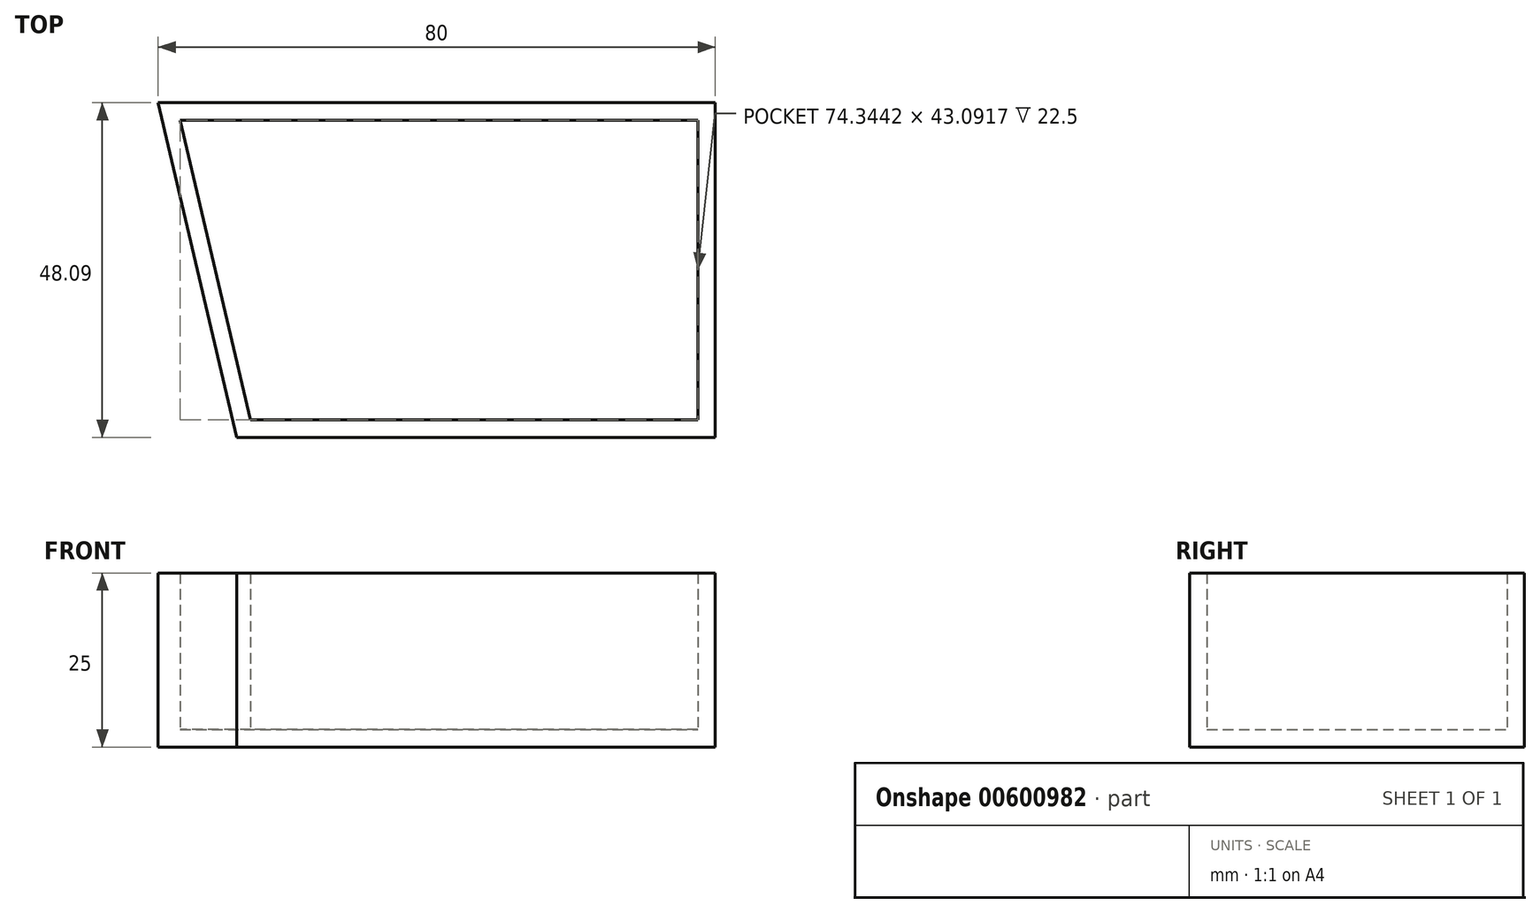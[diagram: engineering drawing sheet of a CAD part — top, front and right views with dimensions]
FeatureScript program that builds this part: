
annotation { "Feature Type Name" : "Feature", "Feature Type Description" : "" }
export const myFeature = defineFeature(function(context is Context, id is Id, definition is map)
    precondition{}
    {
        {
            var Q0;
            Q0=qCreatedBy(makeId("Top.planeOp"),FACE);
            var sketch = newSketch(context, id + "F0", { "sketchPlane" : qUnion([Q0])});
            skLineSegment(sketch, "E0", {"start": v(-43.5, 48.1) * mm, "end": v(36.5, 48.1) * mm});
            skLineSegment(sketch, "E1", {"start": v(36.5, 48.85) * mm, "end": v(36.5, 0) * mm});
            skLineSegment(sketch, "E2", {"start": v(36.5, 0) * mm, "end": v(-32.19, 0) * mm});
            skLineSegment(sketch, "E3", {"start": v(-32.19, 0) * mm, "end": v(-43.5, 48.1) * mm});
            skSolve(sketch);
        }
        {
            var Q0;
            {var subQ0=sQuery(id+"F0.wireOp",EDGE,"E0");Q0=makeQuery(id+"F0.imprint","IMPRINT",FACE,{"disambiguationData":[TD([[makeQuery(id+"F0.imprint","IMPRINT",EDGE,{"derivedFrom":subQ0}),-1.0]])]});}
            extrude(context, id + "F1", {"entities" : qUnion([Q0]), "depth" : 25 * mm, "offsetDistance" : 25 * mm});
        }
        {
            var Q0;
            Q0=makeQuery(id+"F1.opExtrude","CAP_FACE",FACE,{"disambiguationData":[OSD([sQuery(id+"F0.wireOp",EDGE,"E0"),sQuery(id+"F0.wireOp",EDGE,"E1"),sQuery(id+"F0.wireOp",EDGE,"E2"),sQuery(id+"F0.wireOp",EDGE,"E3")])],"isStart":false});
            shell(context, id + "F2", {"entities" : qUnion([Q0]), "thickness" : 2.5 * mm});
        }
    });
